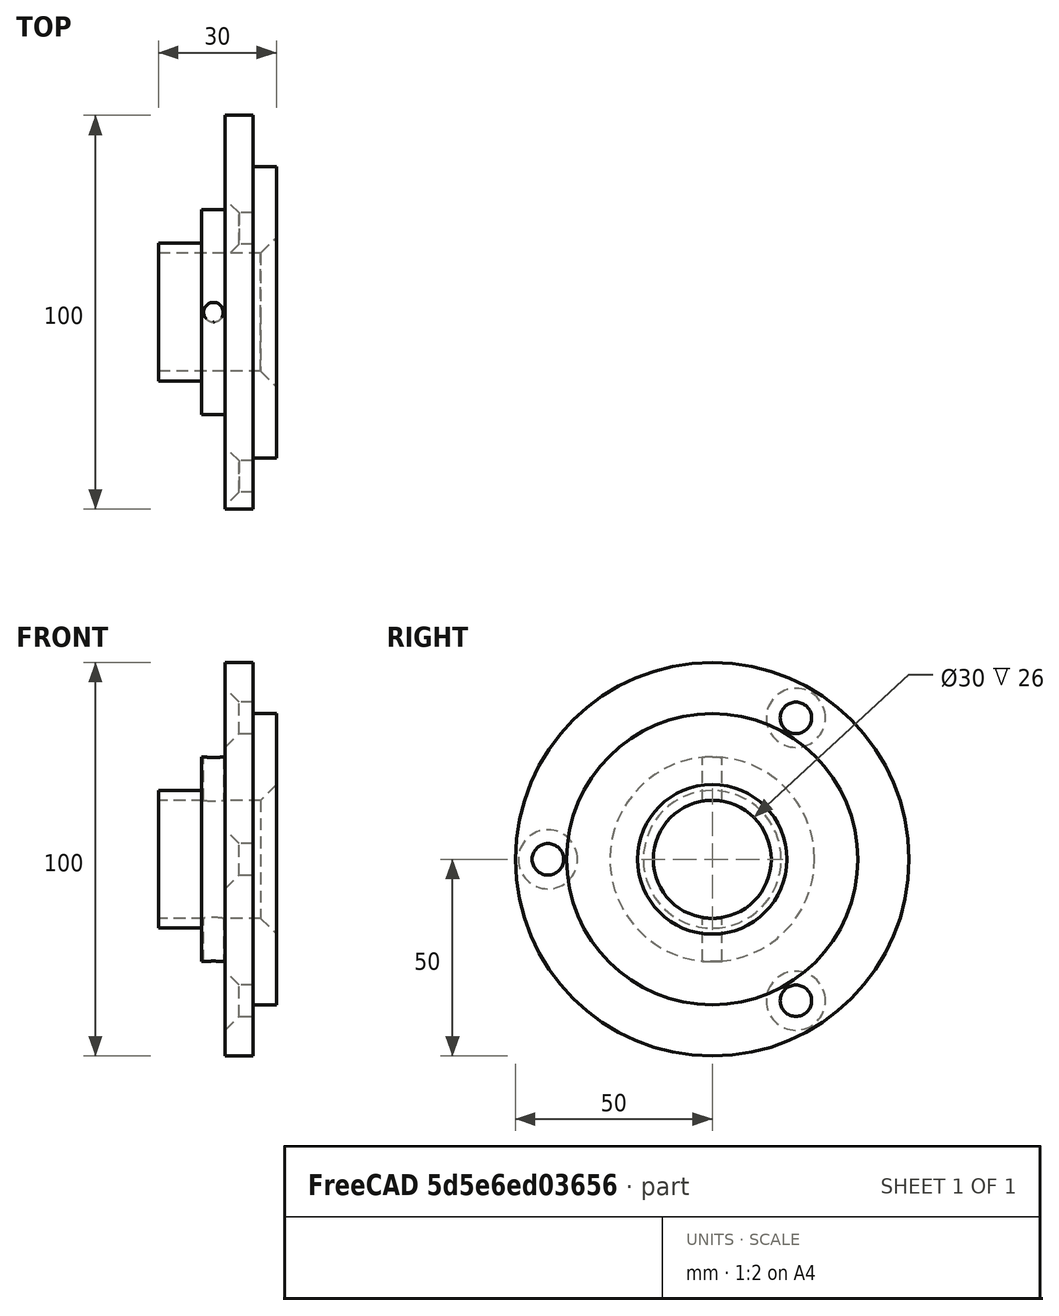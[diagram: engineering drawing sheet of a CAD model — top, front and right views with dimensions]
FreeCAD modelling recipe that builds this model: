
FCSTD DOCUMENT  (FreeCAD 0.21R33771 (Git))
Label: Flagia-Mandrino
License: All rights reserved
LicenseURL: http://en.wikipedia.org/wiki/All_rights_reserved
objects: TechDraw::DrawViewDimension×12, TechDraw::DrawProjGroupItem×4, Sketcher::SketchObject×3, PartDesign::Pocket×2, PartDesign::Chamfer×2, PartDesign::Revolution×1, PartDesign::CoordinateSystem×1, PartDesign::Plane×1, PartDesign::Body×1, TechDraw::DrawSVGTemplate×1, TechDraw::DrawViewSection×1, TechDraw::DrawViewBalloon×1, TechDraw::DrawProjGroup×1, TechDraw::DrawPage×1
note: 33 computed .brp shape members not serialized (recipe doc carries the construction recipe); baked Part::Feature solids carry a one-line shape summary decoded from their .brp

FEATURE [Sketcher::SketchObject] Sketch
  FullyConstrained = true
  MapMode = 5
  Placement = pos=(0,0,0) rot=(1,0,0;1.5708rad)
  Support = -> [XZ_Plane]
  sketch-geometry (10):
    g0: LineSegment StartX=0 StartY=15 StartZ=0 EndX=0 EndY=17.5 EndZ=0
    g1: LineSegment StartX=0 StartY=17.5 StartZ=0 EndX=11 EndY=17.5 EndZ=0
    g2: LineSegment StartX=17 StartY=50 StartZ=0 EndX=24 EndY=50 EndZ=0
    g3: LineSegment StartX=24 StartY=50 StartZ=0 EndX=24 EndY=37 EndZ=0
    g4: LineSegment StartX=24 StartY=37 StartZ=0 EndX=30 EndY=37 EndZ=0
    g5: LineSegment StartX=30 StartY=37 StartZ=0 EndX=30 EndY=15 EndZ=0
    g6: LineSegment StartX=30 StartY=15 StartZ=0 EndX=0 EndY=15 EndZ=0
    g7: LineSegment StartX=17 StartY=50 StartZ=0 EndX=17 EndY=26 EndZ=0
    g8: LineSegment StartX=17 StartY=26 StartZ=0 EndX=11 EndY=26 EndZ=0
    g9: LineSegment StartX=11 StartY=26 StartZ=0 EndX=11 EndY=17.5 EndZ=0
  constraints (30):
    c: PointOnObject(g0,g-2)
    c: PointOnObject(g0,g-2)
    c: Coincident(g1,g0)
    c: Horizontal(g1)
    c: Horizontal(g2)
    c: Vertical(g3)
    c: Horizontal(g4)
    c: Coincident(g5,g4)
    c: Vertical(g5)
    c: Coincident(g6,g5)
    c: Coincident(g6,g0)
    c: Horizontal(g6)
    c: DistanceY(g-1,g0) = 15
    c: Coincident(g3,g2)
    c: Coincident(g3,g4)
    c: DistanceX(g6,g6) = 30
    c: DistanceY(g5,g5) = 22
    c: Coincident(g7,g2)
    c: Vertical(g7)
    c: Coincident(g8,g7)
    c: Horizontal(g8)
    c: Coincident(g9,g8)
    c: Coincident(g9,g1)
    c: Vertical(g9)
    c: DistanceY(g-1,g8) = 26
    c: DistanceX(g8,g8) = 6
    c: DistanceY(g-1,g0) = 17.5
    c: DistanceY(g-1,g2) = 50
    c: DistanceX(g4,g4) = 6
    c: DistanceX(g1,g1) = 11
FEATURE [PartDesign::Revolution] Revolution
  Angle = 360
  Axis = (1,0,0)
  Base = (0,0,0)
  Placement = pos=(0,0,0) rot=(1,0,0;1.5708rad)
  Profile = -> Sketch
  ReferenceAxis = -> X_Axis
FEATURE [Sketcher::SketchObject] Sketch001
  FullyConstrained = false
  MapMode = 5
  Placement = pos=(7,0,0) rot=(0.707107,0,-0.707107;3.14159rad)
  sketch-geometry (5):
    g0: Circle CenterX=0 CenterY=0 CenterZ=0 NormalX=0 NormalY=0 NormalZ=1 AngleXU=0 Radius=41.75
    g1: Circle CenterX=0 CenterY=41.75 CenterZ=0 NormalX=0 NormalY=0 NormalZ=1 AngleXU=0 Radius=4
    g2: Circle CenterX=35.9374 CenterY=-21.25 CenterZ=0 NormalX=0 NormalY=0 NormalZ=1 AngleXU=0 Radius=4
    g3: Circle CenterX=-35.9374 CenterY=-21.25 CenterZ=0 NormalX=0 NormalY=0 NormalZ=1 AngleXU=0 Radius=4
    g4: LineSegment StartX=-66.7657 StartY=-21.25 StartZ=0 EndX=72.4096 EndY=-21.25 EndZ=0
  constraints (13):
    c: Coincident(g0,g-1)
    c: PointOnObject(g1,g0)
    c: PointOnObject(g1,g-2)
    c: Radius(g0) = 41.75
    c: PointOnObject(g2,g0)
    c: PointOnObject(g3,g0)
    c: Horizontal(g4)
    c: PointOnObject(g3,g4)
    c: PointOnObject(g2,g4)
    c: DistanceY(g4,g0) = 21.25
    c: Equal(g1,g3)
    c: Equal(g1,g2)
    c: Radius(g1) = 4
FEATURE [PartDesign::CoordinateSystem] LCS_FllangiaSupportoMandrino  label="LCS_FlangiaSupportoMandrino"
  AttacherType = Attacher::AttachEngine3D
FEATURE [PartDesign::Pocket] Pocket
  BaseFeature = -> Revolution
  Direction = (1,0,2e-16)
  Length = 5
  Length2 = 5
  Placement = pos=(0,0,0) rot=(1,0,0;1.5708rad)
  Profile = -> Sketch001
  ReferenceAxis = -> Sketch001 [N_Axis]
  Type = 1
FEATURE [PartDesign::Chamfer] Chamfer
  Angle = 60
  Base = -> Pocket [Edge7,Edge5,Edge4]
  BaseFeature = -> Pocket
  ChamferType = 0
  FlipDirection = false
  Placement = pos=(0,0,0) rot=(1,0,0;1.5708rad)
  Size = 3.5
  Size2 = 1
  SupportTransform = false
  UseAllEdges = false
FEATURE [PartDesign::Chamfer] Chamfer001
  Angle = 45
  Base = -> Chamfer [Edge28]
  BaseFeature = -> Chamfer
  ChamferType = 0
  FlipDirection = false
  Placement = pos=(0,0,0) rot=(1,0,0;1.5708rad)
  Size = 4
  Size2 = 1
  SupportTransform = false
  UseAllEdges = false
FEATURE [PartDesign::Plane] DatumPlane
  AttachmentOffset = pos=(0,0,50) rot=(0,0,1;0rad)
  Length = 60
  MapMode = 2
  Placement = pos=(0,0,50) rot=(0,0,1;0rad)
  ResizeMode = 0
  Support = -> [XY_Plane]
  Width = 60
FEATURE [Sketcher::SketchObject] Sketch002
  FullyConstrained = true
  MapMode = 5
  Placement = pos=(0,0,50) rot=(0,0,1;0rad)
  Support = -> [DatumPlane]
  sketch-geometry (1):
    g0: Circle CenterX=14 CenterY=0 CenterZ=0 NormalX=0 NormalY=0 NormalZ=1 AngleXU=0 Radius=2.5
  constraints (3):
    c: PointOnObject(g0,g-1)
    c: Radius(g0) = 2.5
    c: DistanceX(g-1,g0) = 14
FEATURE [PartDesign::Pocket] Pocket001
  BaseFeature = -> Chamfer001
  Direction = (0,0,-1)
  Length = 5
  Length2 = 5
  Placement = pos=(0,0,0) rot=(1,0,0;1.5708rad)
  Profile = -> Sketch002
  ReferenceAxis = -> Sketch002 [N_Axis]
  Type = 1
FEATURE [PartDesign::Body] Body
  Group = -> [Sketch,Revolution,Sketch001,LCS_FllangiaSupportoMandrino,Pocket,Chamfer,Chamfer001,DatumPlane,Sketch002,Pocket001]
  Origin = -> Origin
  Tip = -> Pocket001
FEATURE [TechDraw::DrawSVGTemplate] Template
  EditableTexts = Designed_by_Name=Designed by Name; Drawing_number=Drawing number; FC-Date=Date; FC-SC=Scale; FC-SH=Sheet; FC-Title=Flangia Mandrino 03; Subtitle=Acciaio; Weight=Weight
  Height = 210
  Orientation = 1
  Template = <userpath>/Portable/FreeCAD_0.21.2-2023-12-17-conda-Windows-x86_64-py310/data/Mod/TechDraw/Templates/A4_LandscapeTD.svg
  Width = 297
FEATURE [TechDraw::DrawProjGroupItem] ProjItem  label="Front"
  CoarseView = false
  Direction = (-1,0,0)
  Focus = 100
  HardHidden = false
  IsoCount = 0
  IsoHidden = false
  IsoVisible = false
  LockPosition = true
  Perspective = false
  Rotation = 0
  RotationVector = (0,-1,0)
  Scale = 0.7
  ScaleType = 2
  ScrubCount = 0
  SeamHidden = false
  SeamVisible = false
  SmoothHidden = false
  SmoothVisible = true
  Source = -> [Body]
  Type = 0
  X = 0
  XDirection = (0,-1,0)
  Y = 0
FEATURE [TechDraw::DrawProjGroupItem] ProjItem001  label="Left"
  CoarseView = false
  Direction = (-1e-16,1,0)
  Focus = 100
  HardHidden = false
  IsoCount = 0
  IsoHidden = false
  IsoVisible = false
  LockPosition = true
  Perspective = false
  Rotation = 0
  RotationVector = (1,0,0)
  Scale = 0.7
  ScaleType = 2
  ScrubCount = 0
  SeamHidden = false
  SeamVisible = false
  SmoothHidden = false
  SmoothVisible = true
  Source = -> [Body]
  Type = 1
  X = 105.482
  XDirection = (-1,-1e-16,0)
  Y = 0
FEATURE [TechDraw::DrawViewDimension] Dimension001
  AngleOverride = false
  Arbitrary = false
  ArbitraryTolerances = false
  EqualTolerance = true
  ExtensionAngle = 0
  FormatSpec = ⌀%.2w
  FormatSpecOverTolerance = %+.2w
  FormatSpecUnderTolerance = %+.2w
  Inverted = false
  LineAngle = 0
  LockPosition = false
  MeasureType = 1
  OverTolerance = 0
  References2D = -> [ProjItem]
  Rotation = 0
  ScaleType = 0
  TheoreticalExact = false
  Type = 5
  UnderTolerance = 0
  X = 31.937
  Y = 42.9953
FEATURE [TechDraw::DrawViewDimension] Dimension002
  AngleOverride = false
  Arbitrary = false
  ArbitraryTolerances = false
  EqualTolerance = true
  ExtensionAngle = 0
  FormatSpec = ⌀%.2w
  FormatSpecOverTolerance = %+.2w
  FormatSpecUnderTolerance = %+.2w
  Inverted = false
  LineAngle = 0
  LockPosition = false
  MeasureType = 1
  OverTolerance = 0
  References2D = -> [ProjItem]
  Rotation = 0
  ScaleType = 0
  TheoreticalExact = false
  Type = 5
  UnderTolerance = 0
  X = 18.952
  Y = 44.838
FEATURE [TechDraw::DrawViewDimension] Dimension003
  AngleOverride = false
  Arbitrary = false
  ArbitraryTolerances = false
  EqualTolerance = false
  ExtensionAngle = 0
  FormatSpec = ⌀%.2w
  FormatSpecOverTolerance = %+.2w
  FormatSpecUnderTolerance = %+.2w
  Inverted = false
  LineAngle = 0
  LockPosition = false
  MeasureType = 1
  OverTolerance = 0
  References2D = -> [ProjItem]
  Rotation = 0
  ScaleType = 0
  TheoreticalExact = false
  Type = 5
  UnderTolerance = -0.1
  X = 46.7897
  Y = -27.0961
FEATURE [TechDraw::DrawViewDimension] Dimension004
  AngleOverride = false
  Arbitrary = false
  ArbitraryTolerances = false
  EqualTolerance = false
  ExtensionAngle = 0
  FormatSpec = ⌀%.2w
  FormatSpecOverTolerance = %+.2w
  FormatSpecUnderTolerance = %+.2w
  Inverted = false
  LineAngle = 0
  LockPosition = false
  MeasureType = 1
  OverTolerance = 0.1
  References2D = -> [ProjItem]
  Rotation = 0
  ScaleType = 0
  TheoreticalExact = false
  Type = 5
  UnderTolerance = 0
  X = 31.4493
  Y = -31.7766
FEATURE [TechDraw::DrawViewDimension] Dimension005
  AngleOverride = false
  Arbitrary = false
  ArbitraryTolerances = false
  EqualTolerance = true
  ExtensionAngle = 0
  FormatSpec = ⌀%.2w
  FormatSpecOverTolerance = %+.2w
  FormatSpecUnderTolerance = %+.2w
  Inverted = false
  LineAngle = 0
  LockPosition = false
  MeasureType = 1
  OverTolerance = 0
  References2D = -> [ProjItem]
  Rotation = 0
  ScaleType = 0
  TheoreticalExact = false
  Type = 5
  UnderTolerance = 0
  X = -36.1156
  Y = 38.0573
FEATURE [TechDraw::DrawViewDimension] Dimension006
  AngleOverride = false
  Arbitrary = false
  ArbitraryTolerances = false
  EqualTolerance = true
  ExtensionAngle = 0
  FormatSpec = %.2w
  FormatSpecOverTolerance = %+.2w
  FormatSpecUnderTolerance = %+.2w
  Inverted = false
  LineAngle = 0
  LockPosition = false
  MeasureType = 1
  OverTolerance = 0
  References2D = -> [ProjItem001]
  Rotation = 0
  ScaleType = 0
  TheoreticalExact = false
  Type = 1
  UnderTolerance = 0
  X = -33.9986
  Y = 45.2214
FEATURE [TechDraw::DrawViewDimension] Dimension007
  AngleOverride = false
  Arbitrary = false
  ArbitraryTolerances = false
  EqualTolerance = true
  ExtensionAngle = 0
  FormatSpec = %.2w
  FormatSpecOverTolerance = %+.2w
  FormatSpecUnderTolerance = %+.2w
  Inverted = false
  LineAngle = 0
  LockPosition = false
  MeasureType = 1
  OverTolerance = 0
  References2D = -> [ProjItem001]
  Rotation = 0
  ScaleType = 0
  TheoreticalExact = false
  Type = 1
  UnderTolerance = 0
  X = -25.5633
  Y = 51.0968
FEATURE [TechDraw::DrawViewDimension] Dimension008
  AngleOverride = false
  Arbitrary = false
  ArbitraryTolerances = false
  EqualTolerance = true
  ExtensionAngle = 0
  FormatSpec = %.2w
  FormatSpecOverTolerance = %+.2w
  FormatSpecUnderTolerance = %+.2w
  Inverted = false
  LineAngle = 0
  LockPosition = false
  MeasureType = 1
  OverTolerance = 0
  References2D = -> [ProjItem001]
  Rotation = 0
  ScaleType = 0
  TheoreticalExact = false
  Type = 1
  UnderTolerance = 0
  X = -1.1633
  Y = 68.6411
FEATURE [TechDraw::DrawViewDimension] Dimension009
  AngleOverride = false
  Arbitrary = false
  ArbitraryTolerances = false
  EqualTolerance = true
  ExtensionAngle = 0
  FormatSpec = %.2w
  FormatSpecOverTolerance = %+.2w
  FormatSpecUnderTolerance = %+.2w
  Inverted = false
  LineAngle = 0
  LockPosition = false
  MeasureType = 1
  OverTolerance = 0
  References2D = -> [ProjItem001]
  Rotation = 0
  ScaleType = 0
  TheoreticalExact = false
  Type = 1
  UnderTolerance = 0
  X = -20.5242
  Y = 61.0005
FEATURE [TechDraw::DrawViewSection] SectionView  label="Section A - A"
  BaseView = -> ProjItem
  CoarseView = false
  CutSurfaceDisplay = 2
  Direction = (0,-1e-16,-1)
  FileGeomPattern = <userpath>/Portable/FreeCAD_0.21.2-2023-12-17-conda-Windows-x86_64-py310/data/Mod/TechDraw/PAT/FCPAT.pat
  FileHatchPattern = <userpath>/Portable/FreeCAD_0.21.2-2023-12-17-conda-Windows-x86_64-py310/data/Mod/TechDraw/Patterns/simple.svg
  Focus = 100
  FuseBeforeCut = false
  HardHidden = false
  HatchOffset = (0,0,0)
  HatchRotation = 0
  HatchScale = 1
  IsoCount = 0
  IsoHidden = false
  IsoVisible = false
  LockPosition = true
  NameGeomPattern = Diamond
  Perspective = false
  Rotation = 0
  Scale = 0.7
  ScaleType = 2
  ScrubCount = 0
  SeamHidden = false
  SeamVisible = false
  SectionDirection = 4
  SectionNormal = (0,-1e-16,-1)
  SectionOrigin = (15,0,0)
  SectionSymbol = A
  SmoothHidden = false
  SmoothVisible = true
  Source = -> [Body]
  TrimAfterCut = false
  X = 70.37
  XDirection = (0,-1,1e-16)
  Y = 38.4134
FEATURE [TechDraw::DrawProjGroupItem] ProjItem004  label="Bottom"
  CoarseView = false
  Direction = (0,0,-1)
  Focus = 100
  HardHidden = false
  IsoCount = 0
  IsoHidden = false
  IsoVisible = false
  LockPosition = true
  Perspective = false
  Rotation = 0
  RotationVector = (1,0,0)
  ScaleType = 2
  ScrubCount = 0
  SeamHidden = false
  SeamVisible = false
  SmoothHidden = false
  SmoothVisible = true
  Source = -> [Body]
  Type = 5
  X = 0
  XDirection = (0,-1,0)
  Y = 73.8285
FEATURE [TechDraw::DrawViewDimension] Dimension012
  AngleOverride = false
  Arbitrary = false
  ArbitraryTolerances = false
  EqualTolerance = false
  ExtensionAngle = 0
  FormatSpec = ⌀%.2w
  FormatSpecOverTolerance = %+.2w
  FormatSpecUnderTolerance = %+.2w
  Inverted = false
  LineAngle = 0
  LockPosition = false
  MeasureType = 1
  OverTolerance = 0
  References2D = -> [ProjItem001]
  Rotation = 0
  ScaleType = 0
  TheoreticalExact = false
  Type = 2
  UnderTolerance = -0.05
  X = -32.1831
  Y = 3.24561
FEATURE [TechDraw::DrawViewDimension] Dimension014
  AngleOverride = false
  Arbitrary = false
  ArbitraryTolerances = false
  EqualTolerance = true
  ExtensionAngle = 0
  FormatSpec = ⌀%.2w
  FormatSpecOverTolerance = %+.2w
  FormatSpecUnderTolerance = %+.2w
  Inverted = false
  LineAngle = 0
  LockPosition = false
  MeasureType = 1
  OverTolerance = 0
  References2D = -> [ProjItem]
  Rotation = 0
  ScaleType = 0
  TheoreticalExact = false
  Type = 5
  UnderTolerance = 0
  X = -36.179
  Y = 26.3555
FEATURE [TechDraw::DrawViewBalloon] Balloon
  BubbleShape = 0
  EndType = 0
  EndTypeScale = 1
  KinkLength = 5
  LockPosition = false
  OriginX = -2.5
  OriginY = 1
  Rotation = 0
  ScaleType = 0
  ShapeScale = 1
  SourceView = -> ProjItem004
  Text = Filetto M5
  TextWrapLen = -1
  X = 83.0656
  Y = -4.90236
FEATURE [TechDraw::DrawProjGroupItem] ProjItem005  label="FrontBottomRight"
  CoarseView = false
  Direction = (-0.57735,-0.57735,-0.57735)
  Focus = 100
  HardHidden = false
  IsoCount = 0
  IsoHidden = false
  IsoVisible = false
  LockPosition = true
  Perspective = false
  Rotation = 0
  RotationVector = (1,0,0)
  ScaleType = 2
  ScrubCount = 0
  SeamHidden = false
  SeamVisible = false
  SmoothHidden = false
  SmoothVisible = true
  Source = -> [Body]
  Type = 9
  X = 181.142
  XDirection = (0.707107,-0.707107,0)
  Y = 51.4949
FEATURE [TechDraw::DrawProjGroup] ProjGroup
  Anchor = -> ProjItem
  AutoDistribute = true
  LockPosition = false
  ProjectionType = 0
  Rotation = 0
  Scale = 0.7
  ScaleType = 2
  Source = -> [Body]
  Views = -> [ProjItem,ProjItem001,ProjItem004,ProjItem005]
  X = 70.6048
  Y = 106.728
  spacingX = 15
  spacingY = 15
FEATURE [TechDraw::DrawViewDimension] Dimension015
  AngleOverride = false
  Arbitrary = true
  ArbitraryTolerances = false
  EqualTolerance = true
  ExtensionAngle = 0
  FormatSpec = ⌀83,5
  FormatSpecOverTolerance = %+.2w
  FormatSpecUnderTolerance = %+.2w
  Inverted = false
  LineAngle = 0
  LockPosition = false
  MeasureType = 1
  OverTolerance = 0
  References2D = -> [ProjItem]
  Rotation = 0
  ScaleType = 0
  TheoreticalExact = false
  Type = 5
  UnderTolerance = 0
  X = 43.6041
  Y = 32.2197
FEATURE [TechDraw::DrawPage] Page
  KeepUpdated = true
  NextBalloonIndex = 2
  ProjectionType = 0
  Template = -> Template
  Views = -> [ProjGroup,Dimension001,Dimension002,Dimension003,Dimension004,Dimension005,Dimension006,Dimension007,Dimension008,Dimension009,SectionView,Dimension012,Dimension014,Balloon,Dimension015]
